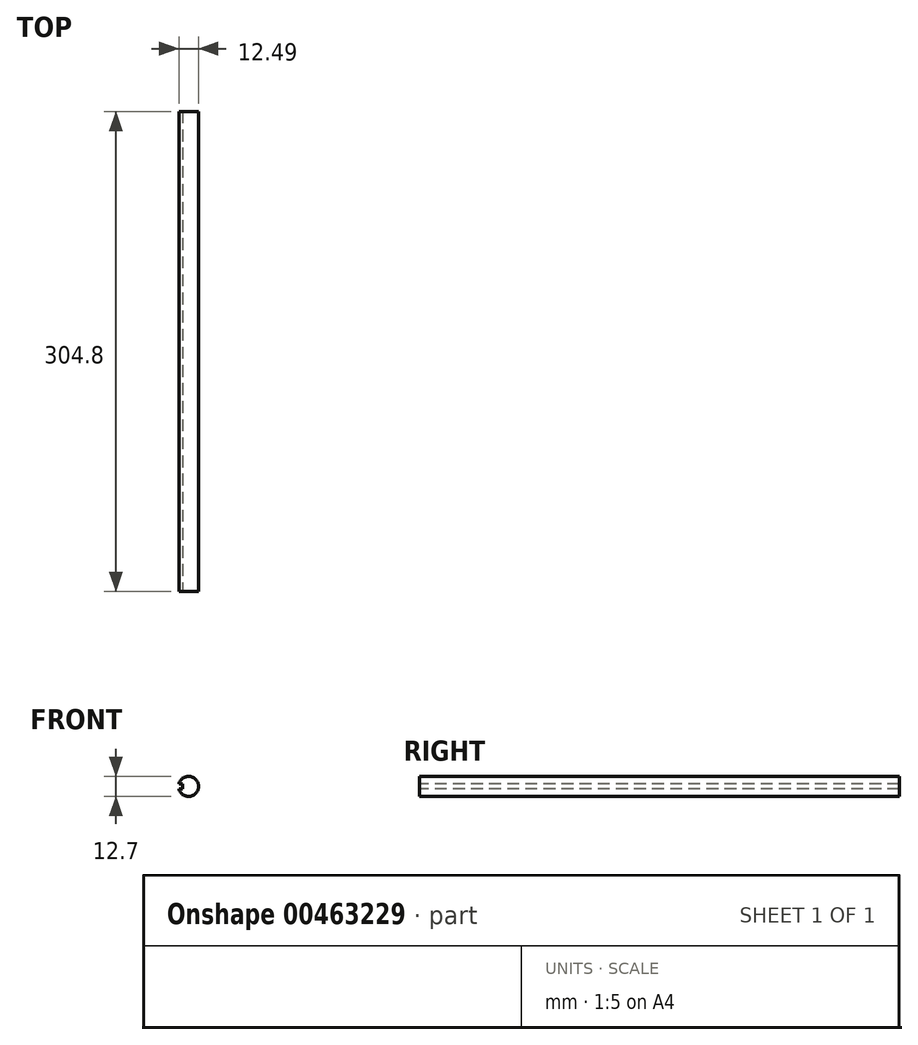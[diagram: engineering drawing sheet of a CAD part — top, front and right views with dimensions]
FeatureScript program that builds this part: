
annotation { "Feature Type Name" : "Feature", "Feature Type Description" : "" }
export const myFeature = defineFeature(function(context is Context, id is Id, definition is map)
    precondition{}
    {
        {
            var Q0;
            Q0=qCreatedBy(makeId("Front.planeOp"),FACE);
            var sketch = newSketch(context, id + "F0", { "sketchPlane" : qUnion([Q0])});
            skArc(sketch, "E0", {"start": v(-6.14, -1.64) * mm, "mid": v(6.35, 0) * mm, "end": v(-6.14, 1.64) * mm});
            skLineSegment(sketch, "E1", {"start": v(-6.14, 1.64) * mm, "end": v(-3.81, 1.64) * mm});
            skLineSegment(sketch, "E2", {"start": v(-6.14, -1.64) * mm, "end": v(-3.81, -1.64) * mm});
            skLineSegment(sketch, "E3", {"start": v(-3.81, 1.64) * mm, "end": v(-3.81, -1.64) * mm});
            skSolve(sketch);
        }
        {
            var Q0;
            Q0=qSketchRegion(id+"F0",true);
            extrude(context, id + "F1", {"entities" : qUnion([Q0]), "oppositeDirection" : true, "depth" : 304.8 * mm});
        }
    });
